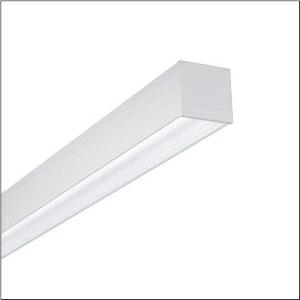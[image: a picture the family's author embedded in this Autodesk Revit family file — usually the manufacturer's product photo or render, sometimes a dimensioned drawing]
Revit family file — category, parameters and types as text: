
# Revit family: silica_r_5mx31bd1e4a_96a8
name_source: partatom
category: Lighting Fixtures
units: mm (PartAtom-declared; Revit-internal decimal feet)

## family parameters
Cut with Voids When Loaded = No
Host = Face
Light Source = No
Part Type = Normal
Room Calculation Point = No
Round Connector Dimension = Use Diameter
Shared = No

## types (1)
- --- (1 x LED, 7070 lm, 45.6 W, 4000K)
    Apparent Load = 46 VA
    CIE Flux Codes = 82 97 100 70 100
    Color Rendering = 80
    Color Temperature = 4000K
    Default Elevation = 1800 mm
    Description = Silica®, office luminaire, of aluminium, light emission: direct/indirect distribution, primary light characteristic: symmetric, installation type: suspended mounting, LED rated luminous flux: 7.070 lm, light colour: 840, colour temperature: 4000K, control gear: ECG DALI, with terminal, 3+2-pole, max. 2.5mm², mains connection: 230V, AC, 50/60Hz, connection cable inclusive, cable length: 1,5 m, rated input power: 46W, luminaire housing, of aluminium, anodised, silver, length: 1.442 mm, width: 65 mm, height: 64mm, protection rating (complete): IP20, insulation class (complete): insulation class I (protective earthing), certification: CE, permissible ambient temperature for indoor applications: 0..+35°C, standard: EN 50419, packaging unit: 1 piece
    Height = 64 mm
    Lamp = 1 x LED
    Lamp Light Flux = 7070 lm
    Lamp Power = 45.6 W
    Lamp count = 1
    Length = 1442 mm
    Luminous efficacy = 155 lm/W
    Manufacturer = Siteco
    ModVariant = No
    Model = 5MX31BD1E4A
    Mounting Place = Ceiling
    Mounting Type = Pendant
    Number of Poles = 1
    OnlyDefault = Yes
    Power Factor = 1
    Product Name = Silica®
    Product group = office luminaire | ceiling pendant
    ProductGroupID = 905
    Protection Class = Protection class I
    Protection Degree = IP 20
    RLX_Detail_Level = 1
    RlxData = <blob elided: 32701 chars, md5=b0720aa3>
    Socket = socket
    Standby Power = 0 W
    System Light Flux = 7070 lm
    System Power = 46 W
    Type Comments = factory setting: direct and indirect light
    Type Image = l_1005409.jpg
    URL = http://relux.com
    VarID = @adj_131724
    Voltage = 0 V
    Weight = 0.00 kg
    Width = 66 mm

## geometry (parser evidence)
native form markers: Blend x4, Sweep x9
no freeform markers — native parametric forms only
